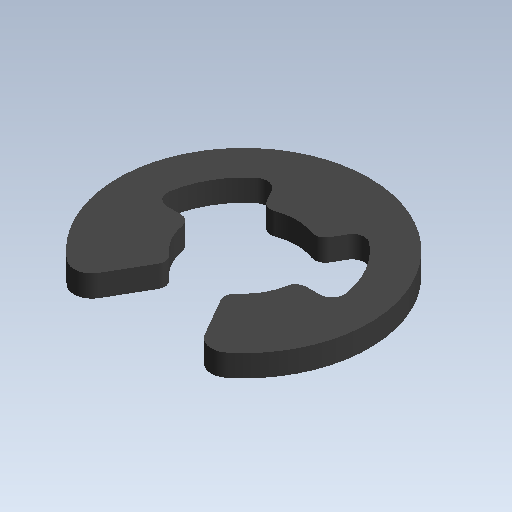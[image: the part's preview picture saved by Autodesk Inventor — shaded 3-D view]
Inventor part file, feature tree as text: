
AUTODESK INVENTOR PART (.ipt)
format: ipt  version: 2020 (Build 240168000, 168)  size: 129,024 bytes
history: native  units: mm (DEFAULTED — no unit token found)
features: other x7, extrude x1, sketch x1
ambient origin geometry x8: Origin, YZ Plane, XZ Plane, XY Plane, X Axis, Y Axis, Z Axis, Center Point
bodies: Solid1 (feature_tree)
feature tree (9):
  extrude  "Extrusion1"  [1 undecoded]
  other  "RR_XY"
  other  "RR_YZ"
  other  "RR_ZX"
  other  "RR_X"
  other  "RR_Y"
  other  "RR_Z"
  other  "RR_Center"
  sketch  "Sketch_1"  dims[d0=1.1049mm d1=0.0mm]
note: 1 required parameter value undecoded (feature->parameter linkage not recoverable at this tier; creation-order binding heuristic only, values carry confidence <= 0.55)
